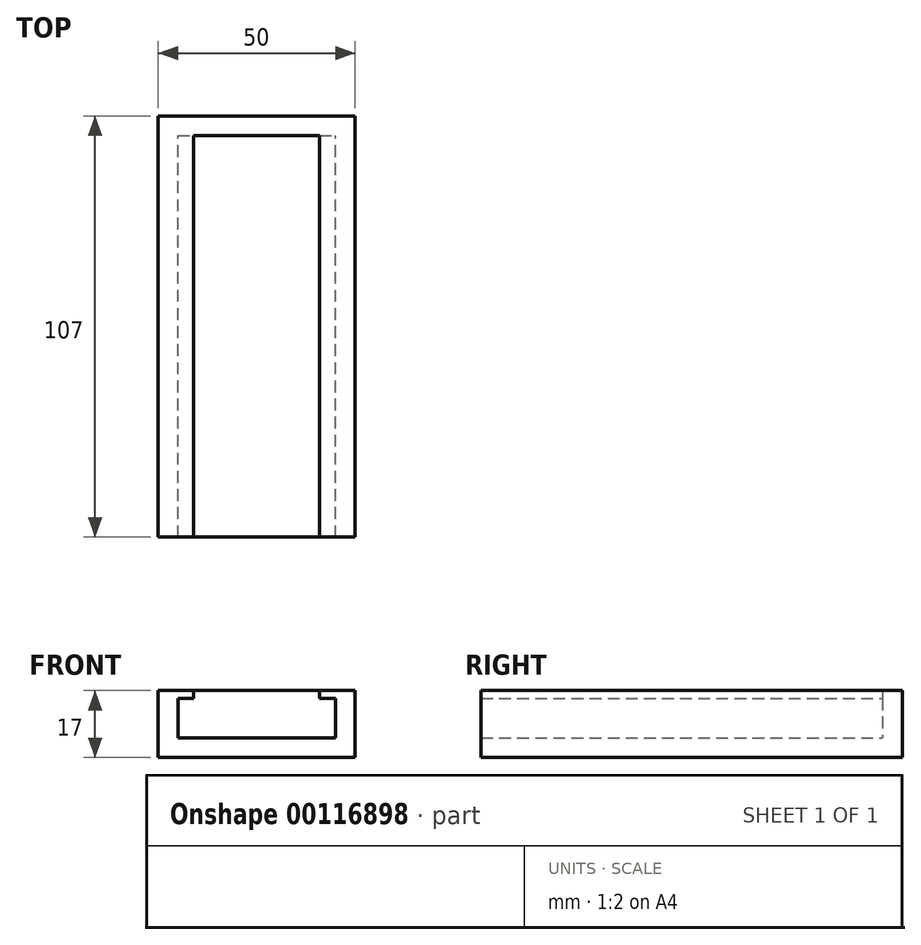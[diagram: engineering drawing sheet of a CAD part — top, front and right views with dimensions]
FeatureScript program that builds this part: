
annotation { "Feature Type Name" : "Feature", "Feature Type Description" : "" }
export const myFeature = defineFeature(function(context is Context, id is Id, definition is map)
    precondition{}
    {
        {
            var Q0;
            Q0=qCreatedBy(makeId("Front.planeOp"),FACE);
            var sketch = newSketch(context, id + "F0", { "sketchPlane" : qUnion([Q0])});
            skLineSegment(sketch, "E0.bottom", {"start": v(-25, 8.5) * mm, "end": v(25, 8.5) * mm});
            skLineSegment(sketch, "E0.top", {"start": v(-25, -8.5) * mm, "end": v(25, -8.5) * mm});
            skLineSegment(sketch, "E0.left", {"start": v(-25, 8.5) * mm, "end": v(-25, -8.5) * mm});
            skLineSegment(sketch, "E0.right", {"start": v(25, 8.5) * mm, "end": v(25, -8.5) * mm});
            skLineSegment(sketch, "E1.bottom", {"start": v(-20, 6.5) * mm, "end": v(20, 6.5) * mm});
            skLineSegment(sketch, "E1.top", {"start": v(-20, -3.5) * mm, "end": v(20, -3.5) * mm});
            skLineSegment(sketch, "E1.left", {"start": v(-20, 6.5) * mm, "end": v(-20, -3.5) * mm});
            skLineSegment(sketch, "E1.right", {"start": v(20, 6.5) * mm, "end": v(20, -3.5) * mm});
            skLineSegment(sketch, "E2", {"start": v(-16, 8.5) * mm, "end": v(-16, 6.5) * mm});
            skLineSegment(sketch, "E3.MirrorCS", {"start": v(16, 8.5) * mm, "end": v(16, 6.5) * mm});
            skSolve(sketch);
        }
        {
            var Q0;
            Q0=makeQuery(id+"F0.imprint","IMPRINT",FACE,{"disambiguationData":[TD([[makeQuery(id+"F0.imprint","IMPRINT",EDGE,{"derivedFrom":sQuery(id+"F0.wireOp",EDGE,"E0.top")}),1.0]])]});
            extrude(context, id + "F1", {"entities" : qUnion([Q0]), "depth" : 102 * mm});
        }
        {
            var Q0;
            Q0=qCreatedBy(makeId("Front.planeOp"),FACE);
            var sketch = newSketch(context, id + "F2", { "sketchPlane" : qUnion([Q0])});
            skLineSegment(sketch, "E4.bottom", {"start": v(25, 8.5) * mm, "end": v(-25, 8.5) * mm});
            skLineSegment(sketch, "E4.top", {"start": v(25, -8.5) * mm, "end": v(-25, -8.5) * mm});
            skLineSegment(sketch, "E4.left", {"start": v(25, 8.5) * mm, "end": v(25, -8.5) * mm});
            skLineSegment(sketch, "E4.right", {"start": v(-25, 8.5) * mm, "end": v(-25, -8.5) * mm});
            skPoint(sketch, "E4.middle", {"position": v(0, 0) * mm});
            skSolve(sketch);
        }
        {
            var Q0;
            Q0 = qSketchRegion(id + "F2", true);
            extrude(context, id + "F3", {"entities" : qUnion([Q0]), "operationType" : NewBodyOperationType.ADD, "oppositeDirection" : true, "depth" : 5 * mm});
        }
    });
